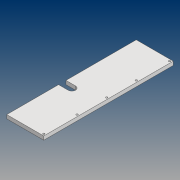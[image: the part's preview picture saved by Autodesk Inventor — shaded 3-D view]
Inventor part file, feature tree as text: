
AUTODESK INVENTOR PART (.ipt)
format: ipt  version: 2021 (Build 250183000, 183)  size: 105,472 bytes
history: native  units: mm
features: other x4, sketch x3, extrude x2, reference x2, hole x1
ambient origin geometry x8: Origin, YZ Plane, XZ Plane, XY Plane, X Axis, Y Axis, Z Axis, Center Point
bodies: Solid1 (feature_tree)
feature tree (12):
  extrude  "Extrusion1"  Depth=100.0mm
  extrude  "Extrusion2"  Depth=20.0mm
  hole  "Hole1"  [1 undecoded]
  sketch  "Sketch1"  dims[d0=350.0mm d1=100.0mm]
  sketch  "Sketch2"  dims[d2=10.0mm d3=0.0mm d4=20.0mm]
  reference  "Reference1"
  reference  "Reference2"
  sketch  "Sketch3"  dims[d5=10.0mm d6=0.0mm d7=5.0mm d8=5.0mm d9=80.0mm d10=5.0mm d11=6.0mm d12=4.0mm d13=2.0mm d14=90.0deg d15=8.0mm d16=20.594885mm]
  other  "0001_ASS_Ban_lap_ghep_01.iam"
  other  "000ASS_Bo_banh_xe_04:1"
  other  "02_Truc_02:1"
  other  "06_Tam_de_01:1"
note: 1 required parameter value undecoded (feature->parameter linkage not recoverable at this tier; creation-order binding heuristic only, values carry confidence <= 0.55)
